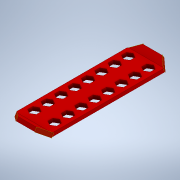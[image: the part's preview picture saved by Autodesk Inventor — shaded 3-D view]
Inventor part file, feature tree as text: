
AUTODESK INVENTOR PART (.ipt)
format: ipt  version: 2020 (Build 240168000, 168)  size: 472,576 bytes
history: native  units: in
note: dims shown in document units (in); Inventor stores cm internally (conversion verified against a paired STEP export)
features: extrude x7, sketch x7, other x4, plane x4
ambient origin geometry x8: Origin, YZ Plane, XZ Plane, XY Plane, X Axis, Y Axis, Z Axis, Center Point
bodies: Solid1 (feature_tree)
feature tree (22):
  other  "HexFlipper.ipt"
  extrude  "Extrusion1"  Depth=0.0787in TaperAngle=0.0deg
  extrude  "Extrusion2"  Depth=0.0787in TaperAngle=0.0deg
  extrude  "Extrusion3"  TaperAngle=135.0deg  [1 undecoded]
  plane  "Work Plane1"
  extrude  "Extrusion4"  Depth=0.9518in TaperAngle=0.0deg
  plane  "Work Plane2"
  extrude  "Extrusion5"  TaperAngle=135.0deg  [1 undecoded]
  plane  "Work Plane3"
  extrude  "Extrusion6"  TaperAngle=0.0deg  [1 undecoded]
  plane  "Work Plane4"
  extrude  "Extrusion7"  [1 undecoded]
  other  "TaggingFeature1"
  sketch  "Sketch1"  dims[d0=0.3937in d1=0.0787in d2=0.0in]
  sketch  "Sketch2"  dims[d3=0.0787in d4=0.0in d5=0.0787in d6=0.0in]
  sketch  "Sketch3"  dims[d7=45.0deg d8=135.0deg]
  sketch  "Sketch4"  dims[d9=0.8199in d10=0.0in d11=0.9518in d12=0.0in]
  sketch  "Sketch5"  dims[d13=45.0deg d14=135.0deg]
  sketch  "Sketch6"  dims[d15=0.0in d16=0.0in d17=0.0in d18=0.0in]
  sketch  "Sketch7"
  other  "Solid1::HexFlipper.ipt"
  other  "Srf1"
note: 4 required parameter values undecoded (feature->parameter linkage not recoverable at this tier; creation-order binding heuristic only, values carry confidence <= 0.55)
